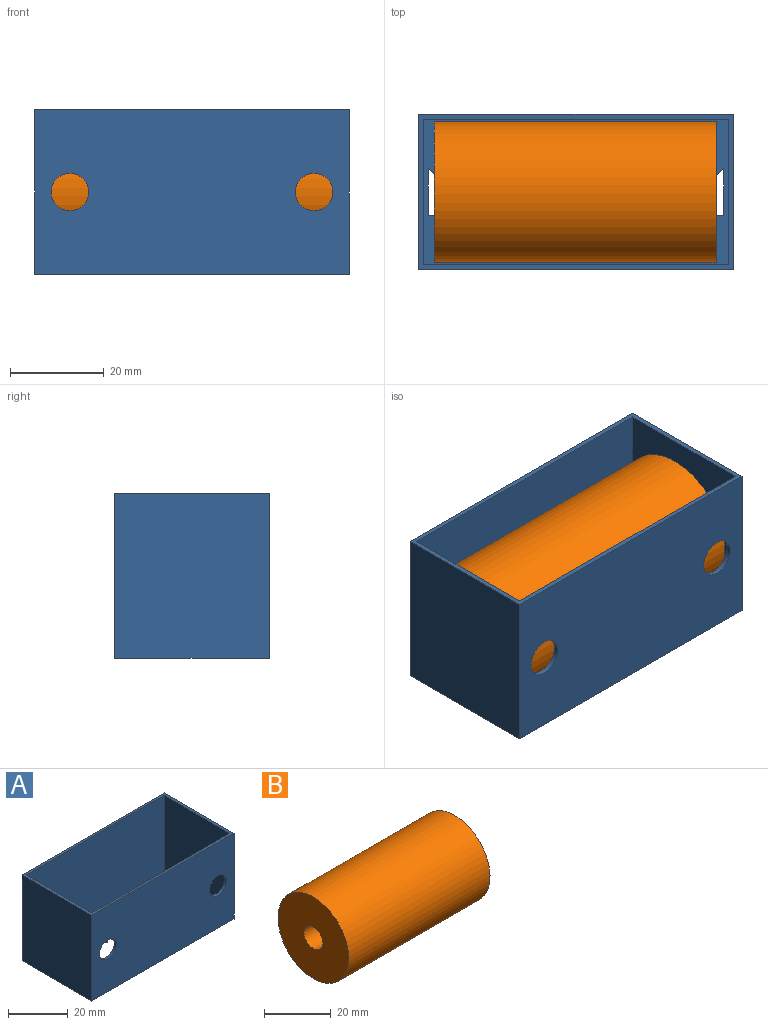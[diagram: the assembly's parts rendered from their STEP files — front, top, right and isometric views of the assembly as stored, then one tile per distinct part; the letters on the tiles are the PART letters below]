
ASSEMBLY  parts=2 mates=2
PART A: 58 faces, bbox 67x33x35 mm
  f0: plane 67x35mm, normal (0,-1,0), area 2244.5mm2, adj f2,f3,f4,f5,f56,f57
  f1: plane 65x34mm, normal (0,1,0), area 2109.5mm2, adj f2,f7,f8,f9,f56,f57
  f2: plane 67x33mm, normal (0,0,1), area 196mm2, adj f0,f1,f4,f5,f6,f8,f9,f10
  f3: plane 67x33mm, normal (0,0,-1), area 1628.3mm2, adj f0,f4,f5,f6,f11,f12,f13,f14
  f4: plane 35x33mm, normal (1,0,0), area 1155mm2, adj f0,f2,f3,f6
  f5: plane 35x33mm, normal (-1,0,0), area 1155mm2, adj f0,f2,f3,f6
  f6: plane 67x35mm, normal (0,1,0), area 2345mm2, adj f2,f3,f4,f5
  f7: plane 65x31mm, normal (0,0,1), area 1432.2mm2, adj f1,f8,f9,f10,f11,f12,f13,f14
  f8: plane 34x31mm, normal (-1,0,0), area 1054mm2, adj f1,f2,f7,f10
  f9: plane 34x31mm, normal (1,0,0), area 1054mm2, adj f1,f2,f7,f10
  f10: plane 65x34mm, normal (0,-1,0), area 2210mm2, adj f2,f7,f8,f9
  f11: plane 10x1mm, normal (-1,0,0), area 10mm2, adj f3,f7,f12,f55
  f12: plane 63x1mm, normal (0,1,0), area 63mm2, adj f3,f7,f11,f13
  f13: plane 10x1mm, normal (1,0,0), area 10mm2, adj f3,f7,f12,f14
  f14: plane 1.5x1.5mm, normal (-0.71,-0.71,0), area 2.1mm2, adj f3,f7,f13,f15
  f15: plane 1.5x1.5mm, normal (0.71,-0.71,0), area 2.1mm2, adj f3,f7,f14,f16
  f16: plane 1.5x1.5mm, normal (-0.71,-0.71,0), area 2.1mm2, adj f3,f7,f15,f17
  f17: plane 1.5x1.5mm, normal (0.71,-0.71,0), area 2.1mm2, adj f3,f7,f16,f18
  f18: plane 1.5x1.5mm, normal (-0.71,-0.71,0), area 2.1mm2, adj f3,f7,f17,f19
  f19: plane 1.5x1.5mm, normal (0.71,-0.71,0), area 2.1mm2, adj f3,f7,f18,f20
  f20: plane 1.5x1.5mm, normal (-0.71,-0.71,0), area 2.1mm2, adj f3,f7,f19,f21
  f21: plane 1.5x1.5mm, normal (0.71,-0.71,0), area 2.1mm2, adj f3,f7,f20,f22
  f22: plane 1.5x1.5mm, normal (-0.71,-0.71,0), area 2.1mm2, adj f3,f7,f21,f23
  f23: plane 1.5x1.5mm, normal (0.71,-0.71,0), area 2.1mm2, adj f3,f7,f22,f24
  f24: plane 1.5x1.5mm, normal (-0.71,-0.71,0), area 2.1mm2, adj f3,f7,f23,f25
  f25: plane 1.5x1.5mm, normal (0.71,-0.71,0), area 2.1mm2, adj f3,f7,f24,f26
  f26: plane 1.5x1.5mm, normal (-0.71,-0.71,0), area 2.1mm2, adj f3,f7,f25,f27
  f27: plane 1.5x1.5mm, normal (0.71,-0.71,0), area 2.1mm2, adj f3,f7,f26,f28
  f28: plane 1.5x1.5mm, normal (-0.71,-0.71,0), area 2.1mm2, adj f3,f7,f27,f29
  f29: plane 1.5x1.5mm, normal (0.71,-0.71,0), area 2.1mm2, adj f3,f7,f28,f30
  f30: plane 1.5x1.5mm, normal (-0.71,-0.71,0), area 2.1mm2, adj f3,f7,f29,f31
  f31: plane 1.5x1.5mm, normal (0.71,-0.71,0), area 2.1mm2, adj f3,f7,f30,f32
  f32: plane 1.5x1.5mm, normal (-0.71,-0.71,0), area 2.1mm2, adj f3,f7,f31,f33
  f33: plane 1.5x1.5mm, normal (0.71,-0.71,0), area 2.1mm2, adj f3,f7,f32,f34
  f34: plane 1.5x1.5mm, normal (-0.71,-0.71,0), area 2.1mm2, adj f3,f7,f33,f35
  f35: plane 1.5x1.5mm, normal (0.71,-0.71,0), area 2.1mm2, adj f3,f7,f34,f36
  f36: plane 1.5x1.5mm, normal (-0.71,-0.71,0), area 2.1mm2, adj f3,f7,f35,f37
  f37: plane 1.5x1.5mm, normal (0.71,-0.71,0), area 2.1mm2, adj f3,f7,f36,f38
  f38: plane 1.5x1.5mm, normal (-0.71,-0.71,0), area 2.1mm2, adj f3,f7,f37,f39
  f39: plane 1.5x1.5mm, normal (0.71,-0.71,0), area 2.1mm2, adj f3,f7,f38,f40
  f40: plane 1.5x1.5mm, normal (-0.71,-0.71,0), area 2.1mm2, adj f3,f7,f39,f41
  f41: plane 1.5x1.5mm, normal (0.71,-0.71,0), area 2.1mm2, adj f3,f7,f40,f42
  f42: plane 1.5x1.5mm, normal (-0.71,-0.71,0), area 2.1mm2, adj f3,f7,f41,f43
  f43: plane 1.5x1.5mm, normal (0.71,-0.71,0), area 2.1mm2, adj f3,f7,f42,f44
  f44: plane 1.5x1.5mm, normal (-0.71,-0.71,0), area 2.1mm2, adj f3,f7,f43,f45
  f45: plane 1.5x1.5mm, normal (0.71,-0.71,0), area 2.1mm2, adj f3,f7,f44,f46
  f46: plane 1.5x1.5mm, normal (-0.71,-0.71,0), area 2.1mm2, adj f3,f7,f45,f47
  f47: plane 1.5x1.5mm, normal (0.71,-0.71,0), area 2.1mm2, adj f3,f7,f46,f48
  f48: plane 1.5x1.5mm, normal (-0.71,-0.71,0), area 2.1mm2, adj f3,f7,f47,f49
  f49: plane 1.5x1.5mm, normal (0.71,-0.71,0), area 2.1mm2, adj f3,f7,f48,f50
  f50: plane 1.5x1.5mm, normal (-0.71,-0.71,0), area 2.1mm2, adj f3,f7,f49,f51
  f51: plane 1.5x1.5mm, normal (0.71,-0.71,0), area 2.1mm2, adj f3,f7,f50,f52
  f52: plane 1.5x1.5mm, normal (-0.71,-0.71,0), area 2.1mm2, adj f3,f7,f51,f53
  f53: plane 1.5x1.5mm, normal (0.71,-0.71,0), area 2.1mm2, adj f3,f7,f52,f54
  f54: plane 1.5x1.5mm, normal (-0.71,-0.71,0), area 2.1mm2, adj f3,f7,f53,f55
  f55: plane 1.5x1.5mm, normal (0.71,-0.71,0), area 2.1mm2, adj f3,f7,f11,f54
  f56: cylinder r=4mm len=8mm, axis (0,-1,0), area 25.1mm2, adj f0,f1
  f57: cylinder r=4mm len=8mm, axis (0,-1,0), area 25.1mm2, adj f0,f1
PART B: 4 faces, bbox 60x30x30 mm
  f0: cylinder r=15mm len=60mm, axis (-1,0,0), area 5654.9mm2, adj f1,f2
  f1: plane 30x30mm, normal (1,0,0), area 656.6mm2, adj f0,f3
  f2: plane 30x30mm, normal (-1,0,0), area 656.6mm2, adj f0,f3
  f3: cylinder r=4mm len=60mm, axis (1,0,0), area 1508mm2, adj f1,f2
PLACE A t=(-59.12,-38.53,16.02)mm
PLACE B rot(axis=(1,0,0),90deg) t=(-89.3,-22.03,16.02)mm
MATE cylindrical A.f4 <-> B.f0  axis (1,0,0) through (-25.62,-22.03,16.02)mm
MATE parallel B.f0 <-> A.f5  axis (-1,0,0) through (-59.3,-22.03,16.02)mm
